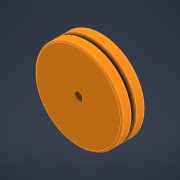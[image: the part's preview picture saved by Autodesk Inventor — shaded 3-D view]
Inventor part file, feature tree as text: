
AUTODESK INVENTOR PART (.ipt)
format: ipt  version: 2021 (Build 250183000, 183)  size: 162,304 bytes
history: native  units: mm
features: fillet x2, revolve x1, sketch x1
ambient origin geometry x8: Origin, YZ Plane, XZ Plane, XY Plane, X Axis, Y Axis, Z Axis, Center Point
bodies: Solid1 (feature_tree)
feature tree (4):
  revolve  "Revolution1"  [1 undecoded]
  fillet  "Fillet2"  Radius=1.5mm
  fillet  "Fillet3"  Radius=3.0mm
  sketch  "Sketch1"  dims[d6=12.0mm d7=12.0mm d10=1.5mm d11=3.0mm d14=90.0deg d15=5.0mm d16=15.0mm d17=50.0mm d18=50.0mm d20=2.0mm d21=1.0mm]
note: 1 required parameter value undecoded (feature->parameter linkage not recoverable at this tier; creation-order binding heuristic only, values carry confidence <= 0.55)
